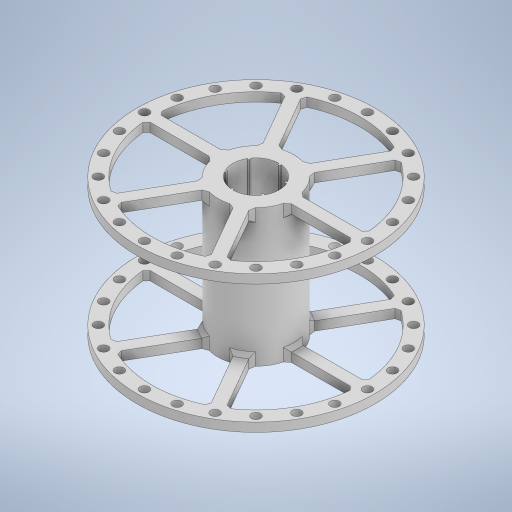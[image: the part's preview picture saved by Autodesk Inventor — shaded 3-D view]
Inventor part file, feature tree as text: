
AUTODESK INVENTOR PART (.ipt)
format: ipt  version: 2024 (Build 280153000, 153)  size: 559,616 bytes
history: native  units: mm
features: extrude x5, sketch x5, pattern_circular x3, chamfer x2, mirror x2, fillet x1
ambient origin geometry x8: Origin, YZ Plane, XZ Plane, XY Plane, X Axis, Y Axis, Z Axis, Center Point
bodies: Volumenkörper1 (feature_tree)
feature tree (18):
  extrude  "Extrusion1"  Depth=25.5mm
  extrude  "Extrusion2"  Depth=46.2mm
  extrude  "Extrusion4"  Depth=3.0mm TaperAngle=0.0deg
  chamfer  "Fasen1"  Distance=3.0mm
  mirror  "Spiegeln2"
  pattern_circular  "Runde Anordnung2"  Angle=45.0deg  [1 undecoded]
  chamfer  "Fasen2"  Distance=60.0mm Angle=360.0deg
  extrude  "Extrusion5"  Depth=0.35mm TaperAngle=45.0deg
  pattern_circular  "Runde Anordnung3"  [2 undecoded]
  mirror  "Spiegeln3"
  extrude  "Extrusion6"  Depth=3.0mm TaperAngle=0.0deg
  pattern_circular  "Runde Anordnung4"  Count=24 Angle=360.0deg
  fillet  "Rundung1"  Radius=0.63mm
  sketch  "Skizze1"  dims[d2=15.5mm d3=25.5mm]
  sketch  "Skizze3"  dims[d4=46.2mm d5=0.0mm d6=70.0mm]
  sketch  "Skizze4"  dims[d7=80.0mm d8=3.0mm d9=0.0mm]
  sketch  "Skizze5"  dims[d13=0.3mm]
  sketch  "Skizze6"  dims[d21=2.0mm d22=3.0mm d23=0.0mm d24=1.25mm d25=2.0mm d26=45.0deg d27=60.0mm d28=360.0deg d30=1.25mm d31=2.0mm d32=45.0deg d33=3.0mm d34=3.0mm d35=0.0mm d36=240.0mm d37=360.0deg d39=0.63mm d40=0.75mm d41=46.2mm d42=0.0mm d43=60.0mm d44=360.0deg d46=0.35mm]
note: 3 required parameter values undecoded (feature->parameter linkage not recoverable at this tier; creation-order binding heuristic only, values carry confidence <= 0.55)
